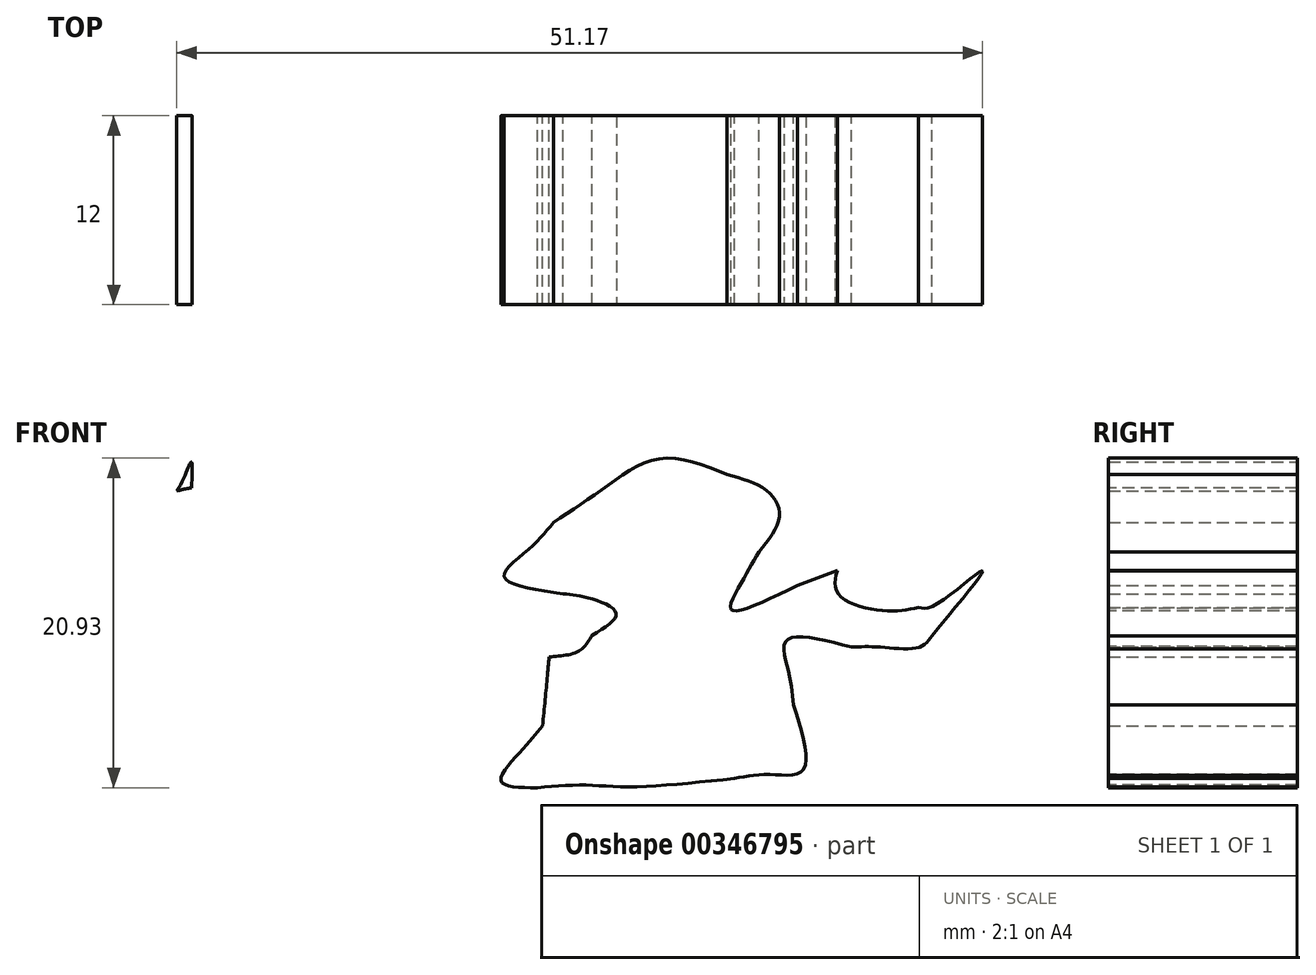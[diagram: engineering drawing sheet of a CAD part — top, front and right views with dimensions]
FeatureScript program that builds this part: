
annotation { "Feature Type Name" : "Feature", "Feature Type Description" : "" }
export const myFeature = defineFeature(function(context is Context, id is Id, definition is map)
    precondition{}
    {
        {
            var Q0;
            Q0=qCreatedBy(makeId("Front.planeOp"),FACE);
            var sketch = newSketch(context, id + "F0", { "sketchPlane" : qUnion([Q0])});
            skFitSpline(sketch, "E0", {"points": [v(6.63, 21.9) * mm, v(8.08, 22.23) * mm, v(9.84, 22.57) * mm, v(10.74, 23.6) * mm]});
            skFitSpline(sketch, "E1", {"points": [v(10.74, 23.6) * mm, v(12.27, 25) * mm, v(10.51, 25.98) * mm, v(8.9, 26.24) * mm]});
            skFitSpline(sketch, "E2", {"points": [v(8.9, 26.24) * mm, v(5.15, 27.35) * mm, v(6.69, 29.06) * mm, v(8.27, 30.77) * mm]});
            skFitSpline(sketch, "E3", {"points": [v(8.27, 30.77) * mm, v(11.58, 33.01) * mm, v(15.02, 34.82) * mm, v(19.32, 33.82) * mm]});
            skFitSpline(sketch, "E4", {"points": [v(19.32, 33.82) * mm, v(21.87, 32.75) * mm, v(22.63, 31.14) * mm, v(21.34, 28.9) * mm]});
            skFitSpline(sketch, "E5", {"points": [v(21.34, 28.9) * mm, v(20.18, 26.89) * mm, v(19.58, 25.24) * mm, v(23.79, 26.78) * mm]});
            skFitSpline(sketch, "E6", {"points": [v(1.56, 57.29) * mm, v(-0.7, 54.99) * mm, v(-2.07, 52.6) * mm, v(-3.16, 50.19) * mm]});
            skFitSpline(sketch, "E7", {"points": [v(-3.16, 50.19) * mm, v(-5.06, 45.3) * mm, v(-2.02, 40.7) * mm, v(3.23, 45.89) * mm]});
            skFitSpline(sketch, "E8", {"points": [v(3.23, 45.89) * mm, v(4.2, 46.72) * mm, v(8.83, 49.4) * mm, v(8.74, 42.46) * mm]});
            skFitSpline(sketch, "E9", {"points": [v(8.74, 42.46) * mm, v(8.86, 37.86) * mm, v(6.78, 33.03) * mm, v(2.98, 35.32) * mm]});
            skFitSpline(sketch, "E10", {"points": [v(2.98, 35.32) * mm, v(0.78, 38.61) * mm, v(-1.65, 37.61) * mm, v(-2.62, 34.23) * mm]});
            skFitSpline(sketch, "E11", {"points": [v(-2.62, 34.23) * mm, v(-4.77, 29.36) * mm, v(-3.52, 24.75) * mm, v(-2.8, 20.09) * mm]});
            skFitSpline(sketch, "E12", {"points": [v(-21.84, 37.36) * mm, v(-21, 37.47) * mm, v(-20.62, 36.88) * mm, v(-19.89, 36.21) * mm]});
            skFitSpline(sketch, "E13", {"points": [v(-19.9, 36.23) * mm, v(-18.04, 35.05) * mm, v(-17.28, 36.9) * mm, v(-16.77, 38.48) * mm]});
            skFitSpline(sketch, "E14", {"points": [v(-16.77, 38.48) * mm, v(-16.1, 42.95) * mm, v(-11.6, 43.36) * mm, v(-9.96, 37.31) * mm]});
            skFitSpline(sketch, "E15", {"points": [v(-9.96, 37.31) * mm, v(-9.58, 35.28) * mm, v(-9.11, 33.25) * mm, v(-10.26, 31.07) * mm]});
            skFitSpline(sketch, "E16", {"points": [v(-10.26, 31.07) * mm, v(-12.16, 27.2) * mm, v(-13.2, 28.44) * mm, v(-15.4, 30.03) * mm]});
            skFitSpline(sketch, "E17", {"points": [v(-15.4, 30.03) * mm, v(-17.97, 31.38) * mm, v(-19.84, 28.93) * mm, v(-18.92, 26) * mm]});
            skFitSpline(sketch, "E18", {"points": [v(-18.92, 26) * mm, v(-17.99, 21.37) * mm, v(-14.38, 19.4) * mm, v(-9.78, 19.09) * mm]});
            skFitSpline(sketch, "E19", {"points": [v(-33.52, 46) * mm, v(-32.09, 46.2) * mm, v(-28.44, 47.13) * mm, v(-27.92, 42.48) * mm]});
            skFitSpline(sketch, "E20", {"points": [v(-27.92, 42.48) * mm, v(-28.06, 38.63) * mm, v(-28.92, 34.41) * mm, v(-24.04, 35.55) * mm]});
            skFitSpline(sketch, "E21", {"points": [v(-24.04, 35.55) * mm, v(-21.57, 36.18) * mm, v(-21.16, 37.55) * mm, v(-22.7, 39.9) * mm]});
            skFitSpline(sketch, "E22", {"points": [v(-22.7, 39.9) * mm, v(-24.21, 42.62) * mm, v(-23.27, 43.94) * mm, v(-20.32, 44.11) * mm]});
            skFitSpline(sketch, "E23", {"points": [v(-20.32, 44.11) * mm, v(-7.1, 60.7) * mm, v(6.75, 62.64) * mm, v(21.52, 44.28) * mm]});
            skLineSegment(sketch, "E24", {"start": v(23.79, 26.78) * mm, "end": v(26.44, 27.76) * mm});
            skFitSpline(sketch, "E25", {"points": [v(25.8, 37.39) * mm, v(28.2, 34.74) * mm, v(30.6, 34.17) * mm, v(27.47, 30.79) * mm]});
            skFitSpline(sketch, "E26", {"points": [v(27.47, 30.79) * mm, v(26.56, 29.61) * mm, v(26.28, 28.57) * mm, v(26.42, 28.07) * mm]});
            skFitSpline(sketch, "E27", {"points": [v(26.42, 28.07) * mm, v(26.34, 26.28) * mm, v(29.16, 25.17) * mm, v(31.48, 25.36) * mm]});
            skFitSpline(sketch, "E28", {"points": [v(31.48, 25.36) * mm, v(32.5, 25.52) * mm, v(35.49, 27.7) * mm, v(32.31, 23.56) * mm]});
            skFitSpline(sketch, "E29", {"points": [v(32.31, 23.56) * mm, v(31.51, 22.84) * mm, v(28.94, 22.86) * mm, v(27.22, 22.85) * mm]});
            skFitSpline(sketch, "E30", {"points": [v(27.22, 22.85) * mm, v(23.08, 23.27) * mm, v(23.2, 21.28) * mm, v(23.54, 19.18) * mm]});
            skFitSpline(sketch, "E31", {"points": [v(23.54, 19.18) * mm, v(24.1, 15) * mm, v(21.94, 14.76) * mm, v(19.78, 14.5) * mm]});
            skFitSpline(sketch, "E32", {"points": [v(19.78, 14.5) * mm, v(13.08, 13.98) * mm, v(10.14, 14.1) * mm, v(7.26, 13.92) * mm]});
            skFitSpline(sketch, "E33", {"points": [v(7.26, 13.92) * mm, v(4.96, 14.37) * mm, v(6.3, 16.34) * mm, v(7.59, 17.84) * mm]});
            skFitSpline(sketch, "E34", {"points": [v(7.59, 17.84) * mm, v(7.98, 23.86) * mm, v(6.64, 21.5) * mm, v(2.54, 21.23) * mm]});
            skLineSegment(sketch, "E35", {"start": v(21.52, 44.28) * mm, "end": v(25.8, 37.39) * mm});
            skFitSpline(sketch, "E36", {"points": [v(-6.1, 19.52) * mm, v(-11.4, 19.25) * mm, v(-9.78, 19.72) * mm, v(-10.73, 15.97) * mm]});
            skFitSpline(sketch, "E37", {"points": [v(-10.71, 16.02) * mm, v(-11.6, 13.63) * mm, v(-13.77, 13.66) * mm, v(-15.6, 13.35) * mm]});
            skLineSegment(sketch, "E38", {"start": v(-6.12, 19.52) * mm, "end": v(-2.82, 20.17) * mm});
            skFitSpline(sketch, "E39", {"points": [v(-26.63, 12.87) * mm, v(-29.3, 12.44) * mm, v(-28.39, 15.07) * mm, v(-27.5, 17.68) * mm]});
            skLineSegment(sketch, "E40", {"start": v(-15.6, 13.35) * mm, "end": v(-26.63, 12.87) * mm});
            skFitSpline(sketch, "E41", {"points": [v(-24.33, 23.15) * mm, v(-22.94, 25.91) * mm, v(-26.15, 26.66) * mm, v(-27.46, 27.07) * mm]});
            skFitSpline(sketch, "E42", {"points": [v(-27.46, 27.07) * mm, v(-34.82, 27.47) * mm, v(-39.7, 29.78) * mm, v(-40.4, 31.42) * mm]});
            skFitSpline(sketch, "E43", {"points": [v(-40.4, 31.42) * mm, v(-41.71, 32.33) * mm, v(-41.64, 34.9) * mm, v(-41.29, 37.8) * mm]});
            skFitSpline(sketch, "E44", {"points": [v(-41.29, 37.8) * mm, v(-41.02, 41.72) * mm, v(-38.35, 44.4) * mm, v(-33.52, 46) * mm]});
            skLineSegment(sketch, "E45", {"start": v(-27.5, 17.68) * mm, "end": v(-24.33, 23.15) * mm});
            skFitSpline(sketch, "E46", {"points": [v(-24.04, 35.55) * mm, v(-21.57, 36.18) * mm, v(-21.16, 37.55) * mm, v(-22.7, 39.9) * mm]});
            skFitSpline(sketch, "E47", {"points": [v(-6.1, 19.52) * mm, v(-11.4, 19.25) * mm, v(-9.78, 19.72) * mm, v(-10.73, 15.97) * mm]});
            skFitSpline(sketch, "E48", {"points": [v(-20.32, 44.11) * mm, v(-7.1, 60.7) * mm, v(6.75, 62.64) * mm, v(21.52, 44.28) * mm]});
            skLineSegment(sketch, "E49", {"start": v(-2.82, 20.17) * mm, "end": v(2.54, 21.23) * mm});
            skFitSpline(sketch, "E50", {"points": [v(7.59, 17.84) * mm, v(7.98, 23.86) * mm, v(6.64, 21.5) * mm, v(2.54, 21.23) * mm]});
            skFitSpline(sketch, "E51", {"points": [v(26.42, 28.07) * mm, v(26.34, 26.28) * mm, v(29.16, 25.17) * mm, v(31.48, 25.36) * mm]});
            skFitSpline(sketch, "E52", {"points": [v(-45.88, -30.28) * mm, v(-45.04, -30.16) * mm, v(-44.65, -30.76) * mm, v(-43.93, -31.42) * mm]});
            skFitSpline(sketch, "E53", {"points": [v(-43.94, -31.4) * mm, v(-42.08, -32.58) * mm, v(-41.32, -30.73) * mm, v(-40.8, -29.15) * mm]});
            skFitSpline(sketch, "E54", {"points": [v(-40.8, -29.15) * mm, v(-40.14, -24.68) * mm, v(-35.64, -24.27) * mm, v(-34, -30.32) * mm]});
            skFitSpline(sketch, "E55", {"points": [v(-34, -30.32) * mm, v(-33.62, -32.35) * mm, v(-33.15, -34.38) * mm, v(-34.3, -36.56) * mm]});
            skFitSpline(sketch, "E56", {"points": [v(-34.3, -36.56) * mm, v(-36.2, -40.43) * mm, v(-37.24, -39.19) * mm, v(-39.43, -37.6) * mm]});
            skFitSpline(sketch, "E57", {"points": [v(-39.43, -37.6) * mm, v(-42, -36.25) * mm, v(-43.88, -38.7) * mm, v(-42.96, -41.64) * mm]});
            skFitSpline(sketch, "E58", {"points": [v(-42.96, -41.64) * mm, v(-42.03, -46.26) * mm, v(-38.42, -48.24) * mm, v(-33.82, -48.55) * mm]});
            skFitSpline(sketch, "E59", {"points": [v(-57.56, -21.64) * mm, v(-56.13, -21.42) * mm, v(-52.48, -20.5) * mm, v(-51.96, -25.15) * mm]});
            skFitSpline(sketch, "E60", {"points": [v(-51.96, -25.15) * mm, v(-52.1, -29) * mm, v(-52.95, -33.22) * mm, v(-48.08, -32.08) * mm]});
            skFitSpline(sketch, "E61", {"points": [v(-48.08, -32.08) * mm, v(-45.61, -31.45) * mm, v(-45.2, -30.08) * mm, v(-46.74, -27.74) * mm]});
            skFitSpline(sketch, "E62", {"points": [v(-34.75, -51.6) * mm, v(-35.64, -54) * mm, v(-37.81, -53.97) * mm, v(-39.64, -54.28) * mm]});
            skFitSpline(sketch, "E63", {"points": [v(-50.66, -54.76) * mm, v(-53.35, -55.2) * mm, v(-52.43, -52.56) * mm, v(-51.54, -49.96) * mm]});
            skLineSegment(sketch, "E64", {"start": v(-39.64, -54.28) * mm, "end": v(-50.66, -54.76) * mm});
            skFitSpline(sketch, "E65", {"points": [v(-48.37, -44.49) * mm, v(-46.98, -41.72) * mm, v(-50.19, -40.97) * mm, v(-51.5, -40.56) * mm]});
            skFitSpline(sketch, "E66", {"points": [v(-51.5, -40.56) * mm, v(-58.85, -40.16) * mm, v(-63.74, -37.85) * mm, v(-64.45, -36.22) * mm]});
            skFitSpline(sketch, "E67", {"points": [v(-64.45, -36.22) * mm, v(-65.75, -35.3) * mm, v(-65.67, -32.73) * mm, v(-65.32, -29.83) * mm]});
            skFitSpline(sketch, "E68", {"points": [v(-65.32, -29.83) * mm, v(-65.06, -25.9) * mm, v(-62.39, -23.22) * mm, v(-57.56, -21.64) * mm]});
            skLineSegment(sketch, "E69", {"start": v(-51.54, -49.96) * mm, "end": v(-48.37, -44.49) * mm});
            skFitSpline(sketch, "E70", {"points": [v(-30.13, -48.1) * mm, v(-35.44, -48.39) * mm, v(-33.82, -47.9) * mm, v(-34.76, -51.66) * mm]});
            skFitSpline(sketch, "E71", {"points": [v(-3.55, 5.02) * mm, v(-5.8, 2.72) * mm, v(-7.18, 0.33) * mm, v(-8.27, -2.08) * mm]});
            skFitSpline(sketch, "E72", {"points": [v(-8.27, -2.08) * mm, v(-10.17, -6.96) * mm, v(-7.13, -11.56) * mm, v(-1.88, -6.38) * mm]});
            skFitSpline(sketch, "E73", {"points": [v(-1.88, -6.38) * mm, v(-0.9, -5.55) * mm, v(3.72, -2.86) * mm, v(3.63, -9.8) * mm]});
            skFitSpline(sketch, "E74", {"points": [v(3.63, -9.8) * mm, v(3.75, -14.4) * mm, v(1.68, -19.24) * mm, v(-2.13, -16.95) * mm]});
            skFitSpline(sketch, "E75", {"points": [v(-2.13, -16.95) * mm, v(-4.33, -13.65) * mm, v(-6.75, -14.65) * mm, v(-7.73, -18.03) * mm]});
            skFitSpline(sketch, "E76", {"points": [v(-7.73, -18.03) * mm, v(-9.88, -22.9) * mm, v(-8.63, -27.52) * mm, v(-7.91, -32.18) * mm]});
            skFitSpline(sketch, "E77", {"points": [v(-26.95, -14.9) * mm, v(-26.11, -14.8) * mm, v(-25.72, -15.4) * mm, v(-25, -16.05) * mm]});
            skFitSpline(sketch, "E78", {"points": [v(-25.01, -16.04) * mm, v(-23.15, -17.21) * mm, v(-22.39, -15.36) * mm, v(-21.88, -13.78) * mm]});
            skFitSpline(sketch, "E79", {"points": [v(-21.88, -13.78) * mm, v(-21.2, -9.31) * mm, v(-16.7, -8.9) * mm, v(-15.07, -14.95) * mm]});
            skFitSpline(sketch, "E80", {"points": [v(-15.07, -14.95) * mm, v(-14.69, -16.99) * mm, v(-14.22, -19.01) * mm, v(-15.37, -21.2) * mm]});
            skFitSpline(sketch, "E81", {"points": [v(-15.37, -21.2) * mm, v(-17.27, -25.06) * mm, v(-18.31, -23.82) * mm, v(-20.5, -22.24) * mm]});
            skFitSpline(sketch, "E82", {"points": [v(-20.5, -22.24) * mm, v(-23.08, -20.88) * mm, v(-24.95, -23.34) * mm, v(-24.03, -26.27) * mm]});
            skFitSpline(sketch, "E83", {"points": [v(-24.03, -26.27) * mm, v(-23.1, -30.9) * mm, v(-19.49, -32.87) * mm, v(-14.89, -33.18) * mm]});
            skFitSpline(sketch, "E84", {"points": [v(-27.81, -12.37) * mm, v(-29.32, -9.64) * mm, v(-28.37, -8.32) * mm, v(-25.43, -8.15) * mm]});
            skFitSpline(sketch, "E85", {"points": [v(-25.43, -8.15) * mm, v(-12.22, 8.43) * mm, v(1.65, 10.38) * mm, v(16.42, -7.99) * mm]});
            skFitSpline(sketch, "E86", {"points": [v(-11.2, -32.74) * mm, v(-16.51, -33.02) * mm, v(-14.89, -32.54) * mm, v(-15.83, -36.3) * mm]});
            skLineSegment(sketch, "E87", {"start": v(-11.23, -32.74) * mm, "end": v(-7.93, -32.1) * mm});
            skFitSpline(sketch, "E88", {"points": [v(-29.15, -16.72) * mm, v(-26.68, -16.09) * mm, v(-26.26, -14.71) * mm, v(-27.81, -12.37) * mm]});
            skFitSpline(sketch, "E89", {"points": [v(16.54, -31.01) * mm, v(17.98, -30.68) * mm, v(19.75, -30.35) * mm, v(20.64, -29.3) * mm]});
            skFitSpline(sketch, "E90", {"points": [v(20.64, -29.3) * mm, v(22.17, -27.91) * mm, v(20.42, -26.94) * mm, v(18.8, -26.68) * mm]});
            skFitSpline(sketch, "E91", {"points": [v(18.8, -26.68) * mm, v(15.06, -25.57) * mm, v(16.6, -23.86) * mm, v(18.18, -22.15) * mm]});
            skFitSpline(sketch, "E92", {"points": [v(18.18, -22.15) * mm, v(21.49, -19.9) * mm, v(24.93, -18.1) * mm, v(29.22, -19.1) * mm]});
            skFitSpline(sketch, "E93", {"points": [v(29.22, -19.1) * mm, v(31.78, -20.16) * mm, v(32.54, -21.77) * mm, v(31.25, -24) * mm]});
            skFitSpline(sketch, "E94", {"points": [v(31.25, -24) * mm, v(30.09, -26.03) * mm, v(29.48, -27.68) * mm, v(33.7, -26.14) * mm]});
            skFitSpline(sketch, "E95", {"points": [v(11.46, 4.37) * mm, v(9.2, 2.07) * mm, v(7.84, -0.32) * mm, v(6.74, -2.73) * mm]});
            skFitSpline(sketch, "E96", {"points": [v(6.74, -2.73) * mm, v(4.84, -7.6) * mm, v(7.89, -12.21) * mm, v(13.13, -7.03) * mm]});
            skFitSpline(sketch, "E97", {"points": [v(13.13, -7.03) * mm, v(14.1, -6.2) * mm, v(18.73, -3.5) * mm, v(18.65, -10.45) * mm]});
            skFitSpline(sketch, "E98", {"points": [v(18.65, -10.45) * mm, v(18.77, -15.06) * mm, v(16.69, -19.89) * mm, v(12.88, -17.6) * mm]});
            skFitSpline(sketch, "E99", {"points": [v(12.88, -17.6) * mm, v(10.68, -14.3) * mm, v(8.26, -15.3) * mm, v(7.29, -18.68) * mm]});
            skFitSpline(sketch, "E100", {"points": [v(7.29, -18.68) * mm, v(5.13, -23.55) * mm, v(6.38, -28.17) * mm, v(7.1, -32.83) * mm]});
            skLineSegment(sketch, "E101", {"start": v(33.7, -26.14) * mm, "end": v(36.34, -25.15) * mm});
            skFitSpline(sketch, "E102", {"points": [v(35.7, -15.53) * mm, v(38.11, -18.17) * mm, v(40.5, -18.74) * mm, v(37.37, -22.13) * mm]});
            skFitSpline(sketch, "E103", {"points": [v(37.37, -22.13) * mm, v(36.46, -23.3) * mm, v(36.18, -24.35) * mm, v(36.33, -24.84) * mm]});
            skFitSpline(sketch, "E104", {"points": [v(36.33, -24.84) * mm, v(36.24, -26.64) * mm, v(39.06, -27.74) * mm, v(41.38, -27.55) * mm]});
            skLineSegment(sketch, "E105", {"start": v(31.43, -8.64) * mm, "end": v(35.7, -15.53) * mm});
            skFitSpline(sketch, "E106", {"points": [v(-10.42, -8.8) * mm, v(2.8, 7.78) * mm, v(16.66, 9.73) * mm, v(31.43, -8.64) * mm]});
            skLineSegment(sketch, "E107", {"start": v(7.09, -32.74) * mm, "end": v(12.44, -31.69) * mm});
            skFitSpline(sketch, "E108", {"points": [v(17.5, -35.07) * mm, v(17.88, -29.06) * mm, v(16.54, -31.42) * mm, v(12.44, -31.69) * mm]});
            skFitSpline(sketch, "E109", {"points": [v(39.25, -41.76) * mm, v(40.7, -41.43) * mm, v(42.46, -41.1) * mm, v(43.35, -40.06) * mm]});
            skFitSpline(sketch, "E110", {"points": [v(43.35, -40.06) * mm, v(44.89, -38.66) * mm, v(43.13, -37.68) * mm, v(41.52, -37.42) * mm]});
            skFitSpline(sketch, "E111", {"points": [v(41.52, -37.42) * mm, v(37.77, -36.31) * mm, v(39.3, -34.6) * mm, v(40.9, -32.9) * mm]});
            skFitSpline(sketch, "E112", {"points": [v(40.9, -32.9) * mm, v(44.2, -30.65) * mm, v(47.64, -28.84) * mm, v(51.94, -29.84) * mm]});
            skFitSpline(sketch, "E113", {"points": [v(51.94, -29.84) * mm, v(54.5, -30.9) * mm, v(55.25, -32.52) * mm, v(53.96, -34.75) * mm]});
            skFitSpline(sketch, "E114", {"points": [v(53.96, -34.75) * mm, v(52.8, -36.77) * mm, v(52.2, -38.43) * mm, v(56.4, -36.88) * mm]});
            skLineSegment(sketch, "E115", {"start": v(56.4, -36.88) * mm, "end": v(59.06, -35.9) * mm});
            skFitSpline(sketch, "E116", {"points": [v(64.1, -38.3) * mm, v(65.1, -38.15) * mm, v(68.1, -35.96) * mm, v(64.93, -40.1) * mm]});
            skFitSpline(sketch, "E117", {"points": [v(64.93, -40.1) * mm, v(64.13, -40.82) * mm, v(61.56, -40.8) * mm, v(59.84, -40.8) * mm]});
            skFitSpline(sketch, "E118", {"points": [v(59.84, -40.8) * mm, v(55.7, -40.4) * mm, v(55.83, -42.38) * mm, v(56.16, -44.48) * mm]});
            skFitSpline(sketch, "E119", {"points": [v(56.16, -44.48) * mm, v(56.72, -48.65) * mm, v(54.56, -48.9) * mm, v(52.4, -49.16) * mm]});
            skFitSpline(sketch, "E120", {"points": [v(52.4, -49.16) * mm, v(45.7, -49.68) * mm, v(42.76, -49.57) * mm, v(39.87, -49.74) * mm]});
            skFitSpline(sketch, "E121", {"points": [v(39.87, -49.74) * mm, v(37.57, -49.3) * mm, v(38.93, -47.32) * mm, v(40.2, -45.82) * mm]});
            skFitSpline(sketch, "E122", {"points": [v(40.2, -45.82) * mm, v(40.6, -39.8) * mm, v(39.26, -42.17) * mm, v(35.15, -42.44) * mm]});
            skFitSpline(sketch, "E123", {"points": [v(59.04, -35.59) * mm, v(58.96, -37.38) * mm, v(61.77, -38.5) * mm, v(64.1, -38.3) * mm]});
            skSolve(sketch);
        }
        {
            var Q0;
            Q0=makeQuery(id+"F0.imprint","IMPRINT",FACE,{"disambiguationData":[TD([[makeQuery(id+"F0.imprint","IMPRINT",EDGE,{"derivedFrom":sQuery(id+"F0.wireOp",EDGE,"E52")}),-1.0]])]});
            var Q1;
            Q1=makeQuery(id+"F0.imprint","IMPRINT",FACE,{"disambiguationData":[TD([[makeQuery(id+"F0.imprint","IMPRINT",EDGE,{"derivedFrom":sQuery(id+"F0.wireOp",EDGE,"E71")}),-1.0]])]});
            var Q2;
            Q2=makeQuery(id+"F0.imprint","IMPRINT",FACE,{"disambiguationData":[TD([[makeQuery(id+"F0.imprint","IMPRINT",EDGE,{"derivedFrom":sQuery(id+"F0.wireOp",EDGE,"E89")}),1.0]])]});
            var Q3;
            Q3=makeQuery(id+"F0.imprint","IMPRINT",FACE,{"disambiguationData":[TD([[makeQuery(id+"F0.imprint","IMPRINT",EDGE,{"derivedFrom":sQuery(id+"F0.wireOp",EDGE,"E109")}),-1.0]])]});
            extrude(context, id + "F1", {"entities" : qUnion([Q0, Q1, Q2, Q3]), "depth" : 12 * mm});
        }
    });
